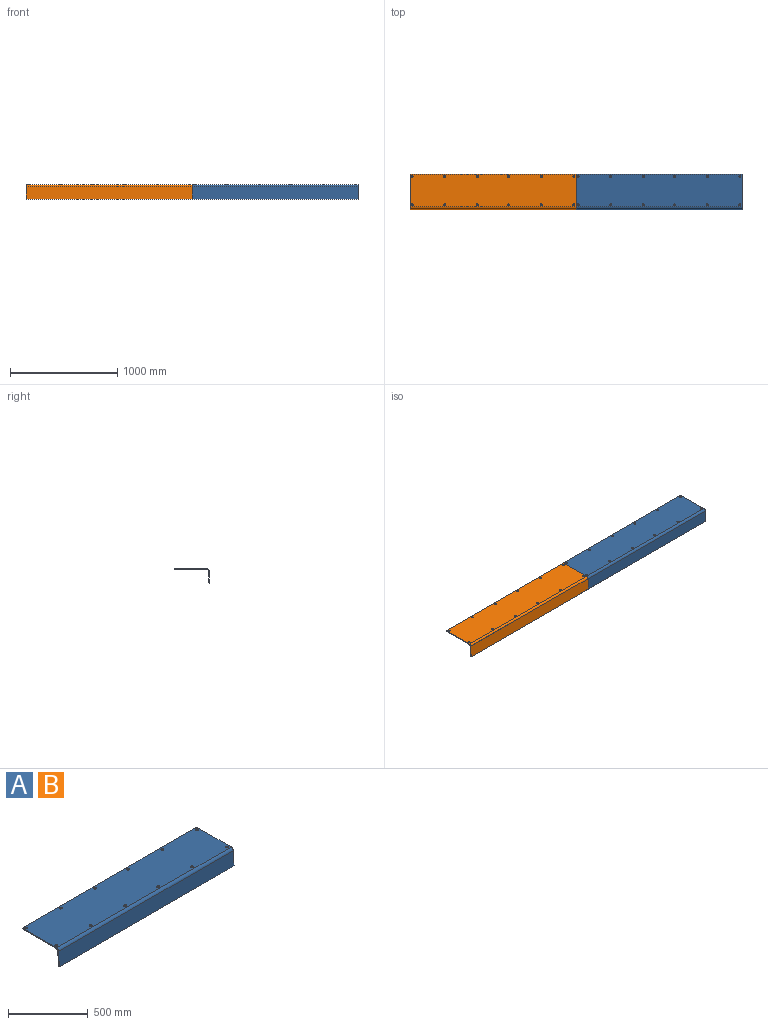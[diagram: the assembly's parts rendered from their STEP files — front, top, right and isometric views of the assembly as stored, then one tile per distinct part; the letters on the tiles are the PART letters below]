
ASSEMBLY  parts=2 mates=1
PART A: 34 faces, bbox 1549.4x330.2x133.4 mm
  f0: plane 1549.4x304.8mm, normal (0,0,-1), area 471204.9mm2, adj f1,f7,f8,f9,f10,f12,f14,f16
  f1: plane 1549.4x6.35mm, normal (0,1,0), area 9838.7mm2, adj f0,f2,f8,f9
  f2: plane 1549.4x304.8mm, normal (0,0,1), area 468836.8mm2, adj f1,f3,f8,f9,f11,f13,f15,f17
  f3: cylinder r=19.05mm len=1549.4mm, axis (-1,0,0), area 44733.1mm2, adj f2,f4,f8,f9
  f4: plane 1549.4x115.35mm, normal (0,-1,0.06), area 178999.3mm2, adj f3,f5,f8,f9
  f5: plane 1549.4x6.36mm, normal (0,0,-1), area 9853.7mm2, adj f4,f6,f8,f9
  f6: plane 1549.4x115mm, normal (0,1,-0.06), area 178455.2mm2, adj f5,f7,f8,f9
  f7: cylinder r=12.7mm len=1549.4mm, axis (-1,0,0), area 29822.1mm2, adj f0,f6,f8,f9
  f8: plane 330.2x133.35mm, normal (1,0,0), area 2820.7mm2, adj f0,f1,f2,f3,f4,f5,f6,f7
  f9: plane 330.2x133.35mm, normal (-1,0,0), area 2820.7mm2, adj f0,f1,f2,f3,f4,f5,f6,f7
  f10: cylinder r=5.28mm len=10.57mm, axis (0,0,1), area 48.8mm2, adj f0,f11
  f11: cone r=5.28mm half-angle=41deg, axis (0,0,1), area 300.8mm2, adj f2,f10
  f12: cylinder r=5.28mm len=10.57mm, axis (0,0,1), area 48.8mm2, adj f0,f13
  f13: cone r=5.28mm half-angle=41deg, axis (0,0,1), area 300.8mm2, adj f2,f12
  f14: cylinder r=5.28mm len=10.57mm, axis (0,0,1), area 48.8mm2, adj f0,f15
  f15: cone r=5.28mm half-angle=41deg, axis (0,0,1), area 300.8mm2, adj f2,f14
  f16: cylinder r=5.28mm len=10.57mm, axis (0,0,1), area 48.8mm2, adj f0,f17
  f17: cone r=5.28mm half-angle=41deg, axis (0,0,1), area 300.8mm2, adj f2,f16
  f18: cylinder r=5.28mm len=10.57mm, axis (0,0,1), area 48.8mm2, adj f0,f19
  f19: cone r=5.28mm half-angle=41deg, axis (0,0,1), area 300.8mm2, adj f2,f18
  f20: cylinder r=5.28mm len=10.57mm, axis (0,0,1), area 48.8mm2, adj f0,f21
  f21: cone r=5.28mm half-angle=41deg, axis (0,0,1), area 300.8mm2, adj f2,f20
  f22: cylinder r=5.28mm len=10.57mm, axis (0,0,1), area 48.8mm2, adj f0,f23
  f23: cone r=5.28mm half-angle=41deg, axis (0,0,1), area 300.8mm2, adj f2,f22
  f24: cylinder r=5.28mm len=10.57mm, axis (0,0,1), area 48.8mm2, adj f0,f25
  f25: cone r=5.28mm half-angle=41deg, axis (0,0,1), area 300.8mm2, adj f2,f24
  f26: cylinder r=5.28mm len=10.57mm, axis (0,0,1), area 48.8mm2, adj f0,f27
  f27: cone r=5.28mm half-angle=41deg, axis (0,0,1), area 300.8mm2, adj f2,f26
  f28: cylinder r=5.28mm len=10.57mm, axis (0,0,1), area 48.8mm2, adj f0,f29
  f29: cone r=5.28mm half-angle=41deg, axis (0,0,1), area 300.8mm2, adj f2,f28
  f30: cylinder r=5.28mm len=10.57mm, axis (0,0,1), area 48.8mm2, adj f0,f31
  f31: cone r=5.28mm half-angle=41deg, axis (0,0,1), area 300.8mm2, adj f2,f30
  f32: cylinder r=5.28mm len=10.57mm, axis (0,0,1), area 48.8mm2, adj f0,f33
  f33: cone r=5.28mm half-angle=41deg, axis (0,0,1), area 300.8mm2, adj f2,f32
PART B: same geometry as A
PLACE A t=(-206.69,41.54,-156.56)mm
PLACE B t=(-1756.09,41.54,-156.56)mm
MATE fastened B.f8 <-> A.f9  axis (1,0,0) through (-206.69,140.62,-175.7)mm
